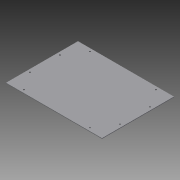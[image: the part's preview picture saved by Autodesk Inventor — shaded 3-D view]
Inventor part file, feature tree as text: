
AUTODESK INVENTOR PART (.ipt)
format: ipt  version: 2015 (Build 190159000, 159)  size: 107,520 bytes
history: native  units: in
note: dims shown in document units (in); Inventor stores cm internally (conversion verified against a paired STEP export)
features: extrude x2, sketch x2
ambient origin geometry x8: Origin, YZ Plane, XZ Plane, XY Plane, X Axis, Y Axis, Z Axis, Center Point
bodies: Solid1 (feature_tree)
feature tree (4):
  extrude  "Extrusion1"  Depth=6.0in
  extrude  "Extrusion2"  Depth=6.0in
  sketch  "Sketch1"  dims[d0=8.0in d1=6.0in]
  sketch  "Sketch3"  dims[d2=0.05in d3=0.0in d36=0.125in d37=0.125in d38=0.125in d39=0.125in d40=0.125in d41=0.125in d42=0.125in d43=0.125in d45=0.25in d46=1.75in d47=0.25in d48=1.25in d49=1.25in d50=0.25in d51=1.75in d52=0.25in d53=1.75in d54=0.25in d55=1.25in d56=0.25in d57=1.25in d58=0.2499in d59=1.75in d60=1.0in d61=0.0in d62=8.0in d63=6.0in]
